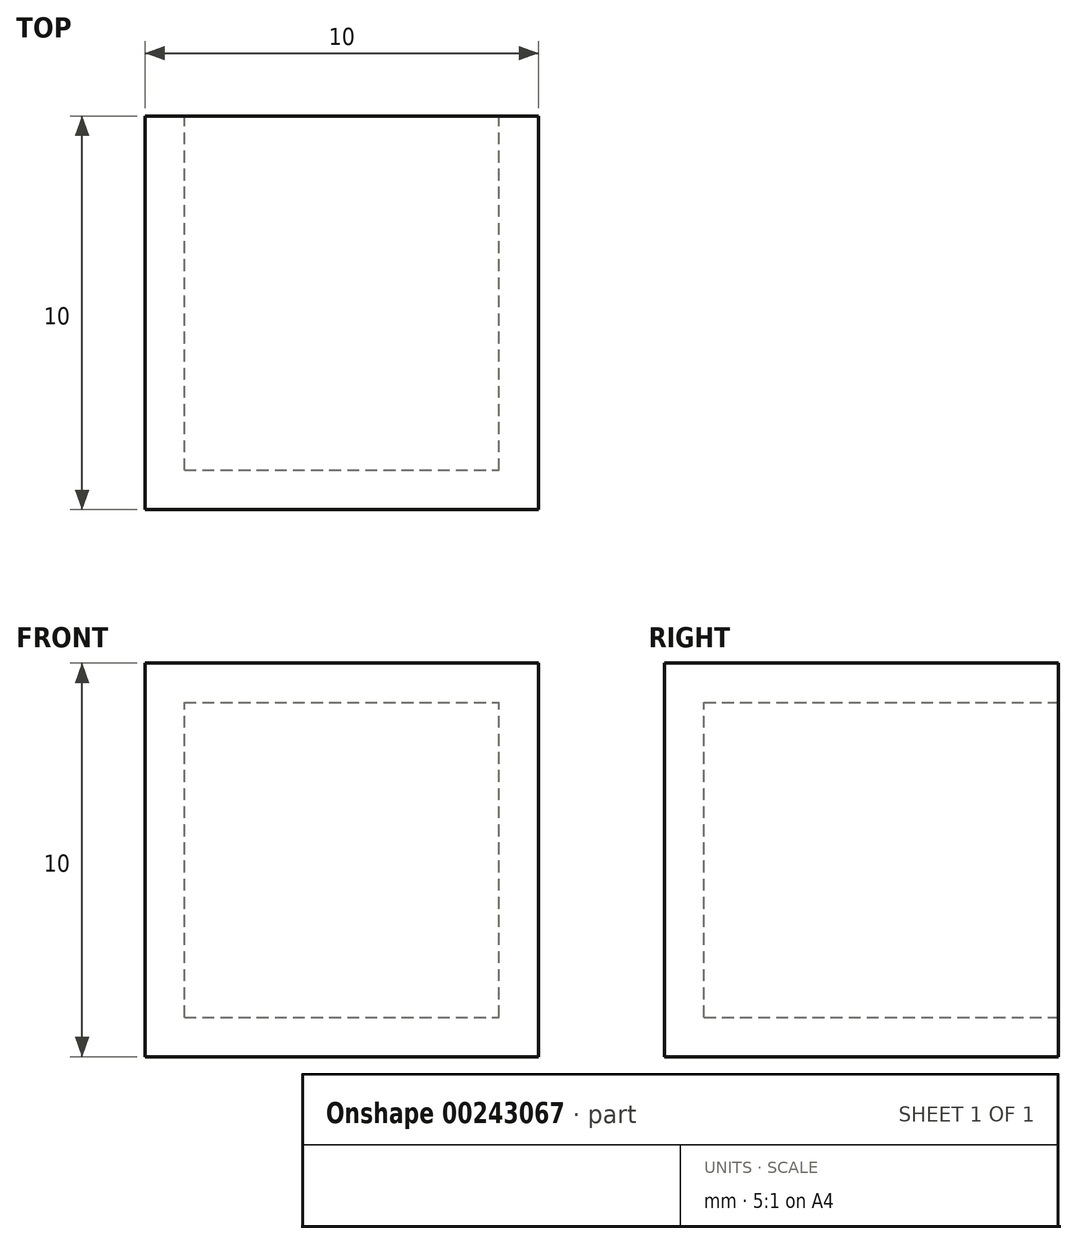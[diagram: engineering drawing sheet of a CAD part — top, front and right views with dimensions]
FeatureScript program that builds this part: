
annotation { "Feature Type Name" : "Feature", "Feature Type Description" : "" }
export const myFeature = defineFeature(function(context is Context, id is Id, definition is map)
    precondition{}
    {
        {
            var Q0;
            Q0=qCreatedBy(makeId("Top.planeOp"),FACE);
            var sketch = newSketch(context, id + "F0", { "sketchPlane" : qUnion([Q0])});
            skLineSegment(sketch, "E0.bottom", {"start": v(0, 0) * mm, "end": v(10, 0) * mm});
            skLineSegment(sketch, "E0.top", {"start": v(0, 10) * mm, "end": v(10, 10) * mm});
            skLineSegment(sketch, "E0.left", {"start": v(0, 0) * mm, "end": v(0, 10) * mm});
            skLineSegment(sketch, "E0.right", {"start": v(10, 0) * mm, "end": v(10, 10) * mm});
            skSolve(sketch);
        }
        {
            var Q0;
            Q0 = qSketchRegion(id + "F0", true);
            extrude(context, id + "F1", {"entities" : qUnion([Q0]), "oppositeDirection" : true, "depth" : 10 * mm});
        }
        {
            var Q0;
            Q0=makeQuery(id+"F1.opExtrude","SWEPT_FACE",FACE,{"disambiguationData":[OSD([sQuery(id+"F0.wireOp",EDGE,"E0.top")])]});
            shell(context, id + "F2", {"entities" : qUnion([Q0]), "thickness" : 1 * mm});
        }
    });
